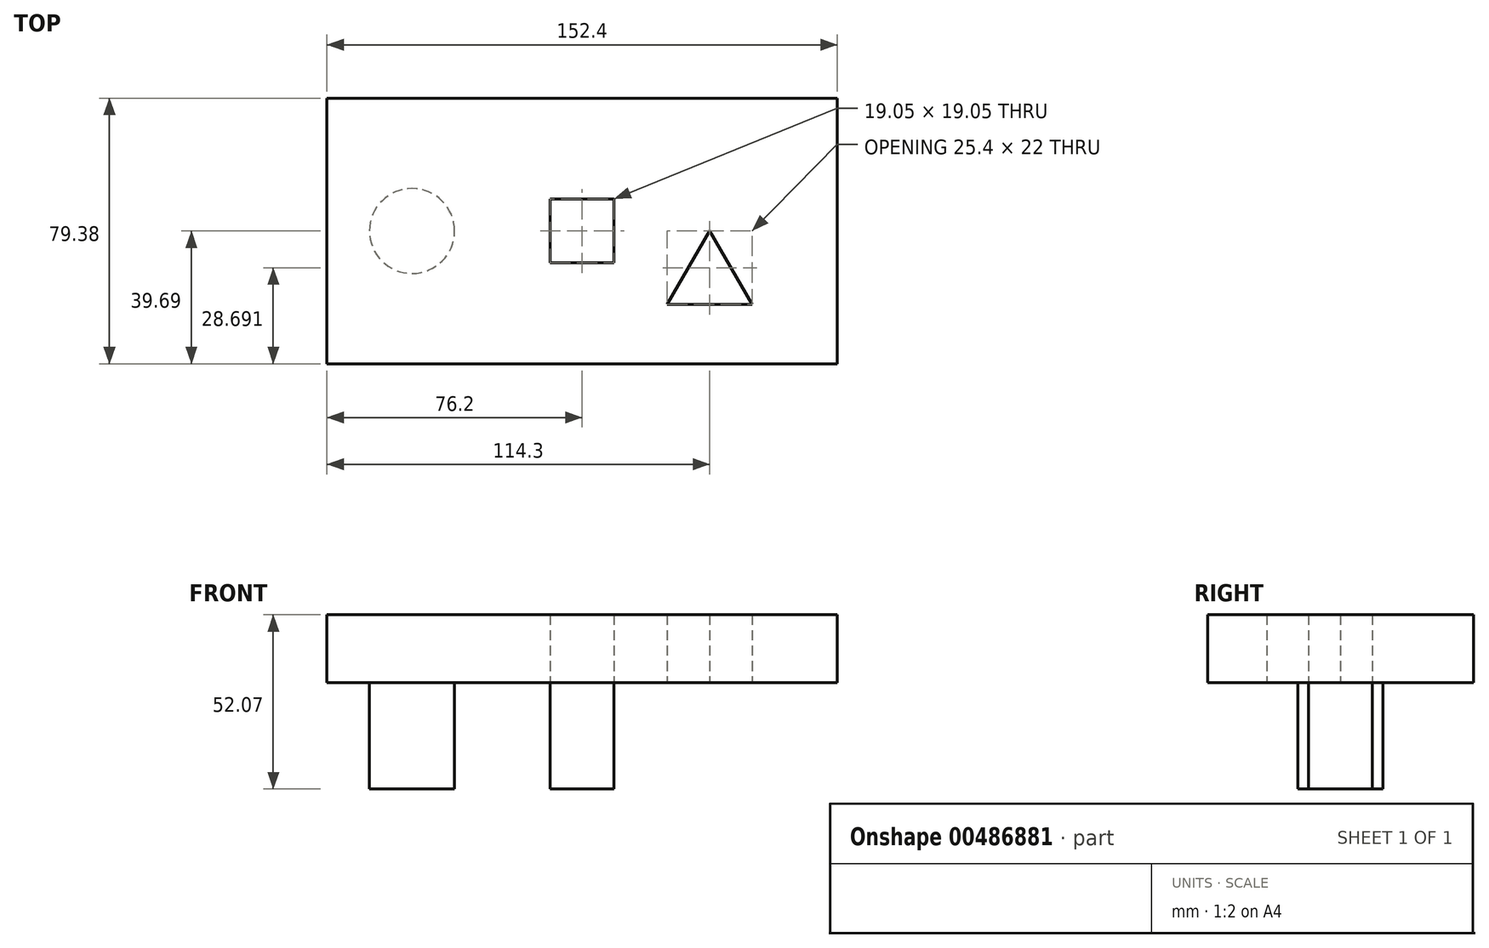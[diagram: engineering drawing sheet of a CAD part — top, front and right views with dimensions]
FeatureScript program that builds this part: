
annotation { "Feature Type Name" : "Feature", "Feature Type Description" : "" }
export const myFeature = defineFeature(function(context is Context, id is Id, definition is map)
    precondition{}
    {
        {
            var Q0;
            Q0=qCreatedBy(makeId("Top.planeOp"),FACE);
            var sketch = newSketch(context, id + "F0", { "sketchPlane" : qUnion([Q0])});
            skLineSegment(sketch, "E0", {"start": v(-6.35, -22) * mm, "end": v(6.35, 0) * mm});
            skLineSegment(sketch, "E1", {"start": v(6.35, 0) * mm, "end": v(19.05, -22) * mm});
            skLineSegment(sketch, "E2", {"start": v(19.05, -22) * mm, "end": v(-6.35, -22) * mm});
            skLineSegment(sketch, "E3.bottom", {"start": v(-22.22, 9.52) * mm, "end": v(-41.27, 9.52) * mm});
            skLineSegment(sketch, "E3.top", {"start": v(-22.22, -9.53) * mm, "end": v(-41.27, -9.53) * mm});
            skLineSegment(sketch, "E3.left", {"start": v(-22.22, 9.52) * mm, "end": v(-22.22, -9.53) * mm});
            skLineSegment(sketch, "E3.right", {"start": v(-41.27, 9.52) * mm, "end": v(-41.27, -9.53) * mm});
            skPoint(sketch, "E3.middle", {"position": v(-31.75, 0) * mm});
            skCircle(sketch, "E4", {"center": v(-82.55, 0) * mm, "radius": 12.7 * mm});
            skLineSegment(sketch, "E5.bottom", {"start": v(44.45, 39.69) * mm, "end": v(-107.95, 39.69) * mm});
            skLineSegment(sketch, "E5.top", {"start": v(44.45, -39.69) * mm, "end": v(-107.95, -39.69) * mm});
            skLineSegment(sketch, "E5.left", {"start": v(44.45, 39.69) * mm, "end": v(44.45, -39.69) * mm});
            skLineSegment(sketch, "E5.right", {"start": v(-107.95, 39.69) * mm, "end": v(-107.95, -39.69) * mm});
            skSolve(sketch);
        }
        {
            var Q0;
            Q0 = qSketchRegion(id + "F0", true);
            var Q1;
            Q1=makeQuery(id+"F0.imprint","IMPRINT",FACE,{"disambiguationData":[TD([[makeQuery(id+"F0.imprint","IMPRINT",EDGE,{"derivedFrom":sQuery(id+"F0.wireOp",EDGE,"E4")}),1.0]])]});
            extrude(context, id + "F1", {"entities" : qUnion([Q0, Q1]), "depth" : 20.32 * mm});
        }
        {
            var Q0;
            Q0=makeQuery(id+"F0.imprint","IMPRINT",FACE,{"disambiguationData":[TD([[makeQuery(id+"F0.imprint","IMPRINT",EDGE,{"derivedFrom":sQuery(id+"F0.wireOp",EDGE,"E4")}),1.0]])]});
            extrude(context, id + "F2", {"entities" : qUnion([Q0]), "operationType" : NewBodyOperationType.ADD, "oppositeDirection" : true, "depth" : 31.75 * mm});
        }
        {
            var Q0;
            Q0=makeQuery(id+"F1.opExtrude","CAP_FACE",FACE,{"disambiguationData":[OSD([sQuery(id+"F0.wireOp",EDGE,"E0"),sQuery(id+"F0.wireOp",EDGE,"E1"),sQuery(id+"F0.wireOp",EDGE,"E2"),sQuery(id+"F0.wireOp",EDGE,"E3.bottom"),sQuery(id+"F0.wireOp",EDGE,"E3.top"),sQuery(id+"F0.wireOp",EDGE,"E3.left"),sQuery(id+"F0.wireOp",EDGE,"E3.right"),sQuery(id+"F0.wireOp",EDGE,"E5.bottom"),sQuery(id+"F0.wireOp",EDGE,"E5.top"),sQuery(id+"F0.wireOp",EDGE,"E5.left"),sQuery(id+"F0.wireOp",EDGE,"E5.right")])],"isStart":true});
            var sketch = newSketch(context, id + "F3", { "sketchPlane" : qUnion([Q0])});
            skSolve(sketch);
        }
        {
            var Q0;
            Q0=makeQuery(id+"F3.imprint","IMPRINT",FACE,{"disambiguationData":[TD([[makeQuery(id+"F3.imprint","IMPRINT",EDGE,{"derivedFrom":makeQuery(id+"F1.opExtrude","CAP_EDGE",EDGE,{"disambiguationData":[OSD([sQuery(id+"F0.wireOp",EDGE,"E3.bottom")])],"isStart":true})}),-1.0]])]});
            extrude(context, id + "F4", {"entities" : qUnion([Q0]), "depth" : 31.75 * mm});
        }
    });
